# Revit family: Sanitary_Taps-Mixers_hansgrohe_75010USA-Vivenis-Single-lever-basin-mixe_NEW
name_source: partatom
category: Plumbing Fixtures
revit_build: Autodesk Revit 2015 (Build: 20140903_1530(x64)
units: mm (PartAtom-declared; Revit-internal decimal feet)

## types (4) — shared parameters
Always visible = Yes
BIMobject category = Taps & Mixers
BIMobject category code = sanitary-taps-mixers
BIMobject main category = Sanitary
BIMobject main category code = sanitary
Brand url = http://www.hansgrohe-int.com
Design country = Germany
Edition number = 1
GTIN code = https://4059625335239
IFC Classification = Sanitary Terminal
Installation instructions = https://www.hansgrohe.com
Manufacturer country = Germany
Manufacturer name = hansgrohe
Material main = Chrome
Product Guid = 9a13ab69-eadb-4a8f-a6fb-ebb356b4a49c
Product SKU = 75010USA
Product data url = https://bimobject.com
Product family = Vivenis
Product group = Basin mixers
Product name = 75010USA Vivenis Single lever basin mixer 80 with pop-up waste set
Product url = https://www.hansgrohe.com
QR code = http://bimobject.com
Technical description = https://www.hansgrohe.com

## per-type parameters (varying)
| type | Material 1 |
| 701 Matt white | Hansgrohe - Vivenis - 701 Matt white |
| 671 Matt black | Hansgrohe - Vivenis - 671 Matt black |
| 821 Brushed Nickel | Hansgrohe - Vivenis - 821 Brushed Nickel |
| 001 Chrome | Hansgrohe - Vivenis - 001 Chrome |

## geometry (parser evidence)
native form markers: Sweep x4
no freeform markers — native parametric forms only
